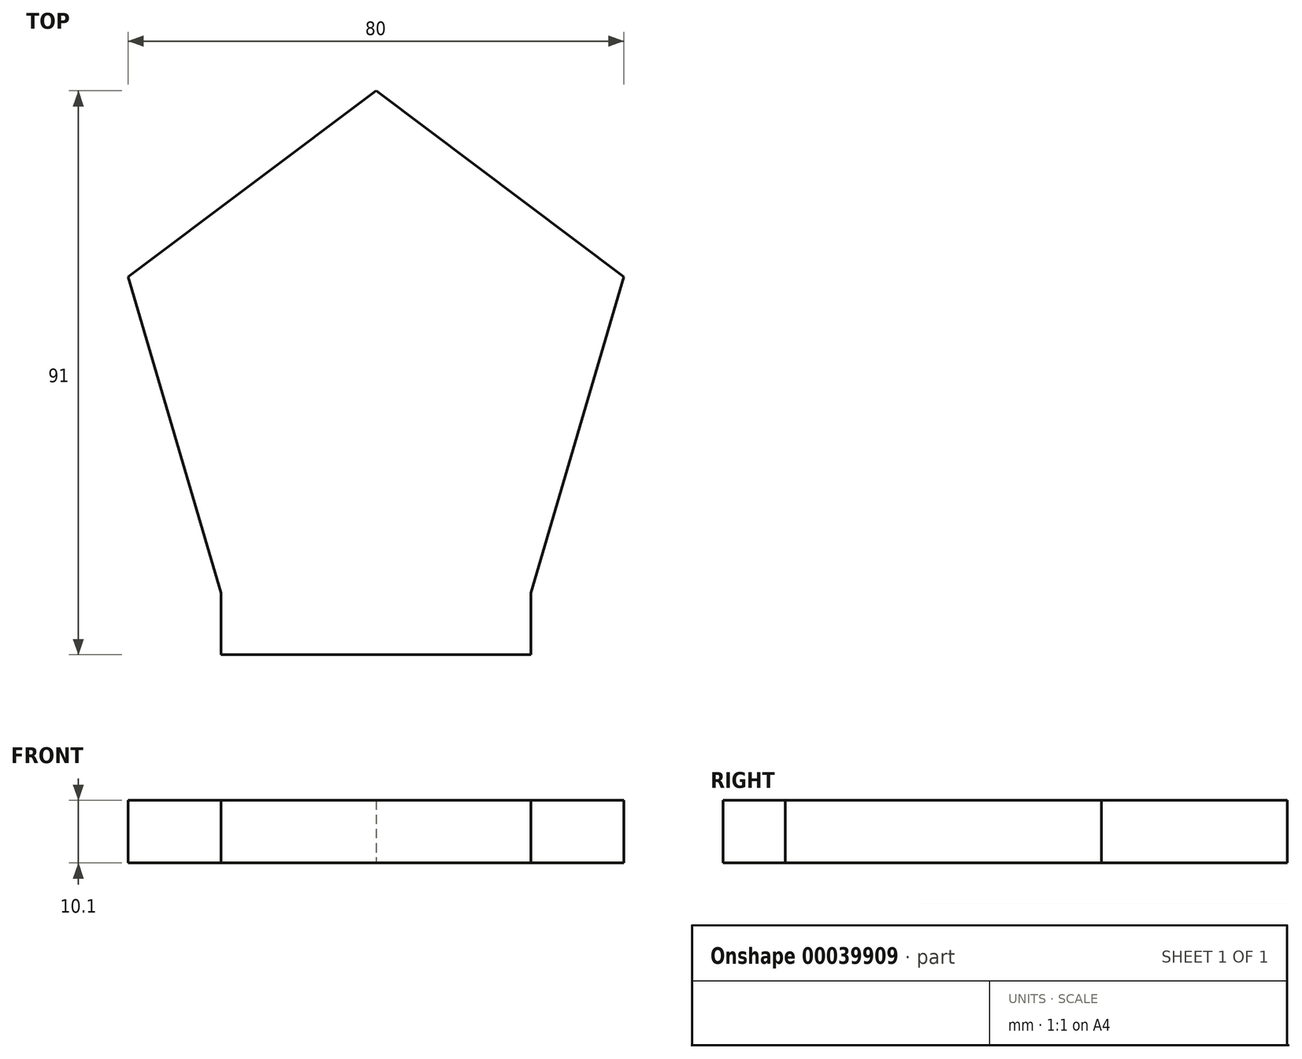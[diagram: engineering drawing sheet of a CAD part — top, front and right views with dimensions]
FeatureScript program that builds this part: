
annotation { "Feature Type Name" : "Feature", "Feature Type Description" : "" }
export const myFeature = defineFeature(function(context is Context, id is Id, definition is map)
    precondition{}
    {
        {
            var Q0;
            Q0=qCreatedBy(makeId("Top.planeOp"),FACE);
            var sketch = newSketch(context, id + "F0", { "sketchPlane" : qUnion([Q0])});
            skLineSegment(sketch, "E0.bottom", {"start": v(-25, -39.07) * mm, "end": v(25, -39.07) * mm});
            skLineSegment(sketch, "E0.top", {"start": v(-25, -49.07) * mm, "end": v(25, -49.07) * mm});
            skLineSegment(sketch, "E0.left", {"start": v(-25, -39.07) * mm, "end": v(-25, -49.07) * mm});
            skLineSegment(sketch, "E0.right", {"start": v(25, -39.07) * mm, "end": v(25, -49.07) * mm});
            skLineSegment(sketch, "E1.top", {"start": v(-25, -69.07) * mm, "end": v(25, -69.07) * mm});
            skLineSegment(sketch, "E1.left", {"start": v(-25, -49.07) * mm, "end": v(-25, -69.07) * mm});
            skLineSegment(sketch, "E1.right", {"start": v(25, -49.07) * mm, "end": v(25, -69.07) * mm});
            skLineSegment(sketch, "E2.bottom", {"start": v(-40, 11.93) * mm, "end": v(40, 11.93) * mm});
            skLineSegment(sketch, "E3", {"start": v(-40, 11.93) * mm, "end": v(-25, -39.07) * mm});
            skLineSegment(sketch, "E4", {"start": v(25, -39.07) * mm, "end": v(40, 11.93) * mm});
            skLineSegment(sketch, "E5", {"start": v(-40, 11.93) * mm, "end": v(0, 41.93) * mm});
            skLineSegment(sketch, "E6", {"start": v(0, 41.93) * mm, "end": v(40, 11.93) * mm});
            skLineSegment(sketch, "E7", {"start": v(0, 41.93) * mm, "end": v(0, 11.93) * mm, "construction": true});
            skLineSegment(sketch, "E8", {"start": v(0, 11.93) * mm, "end": v(0, -39.07) * mm, "construction": true});
            skSolve(sketch);
        }
        {
            var Q0;
            Q0=makeQuery(id+"F0.imprint","IMPRINT",FACE,{"disambiguationData":[TD([[makeQuery(id+"F0.imprint","IMPRINT",EDGE,{"derivedFrom":sQuery(id+"F0.wireOp",EDGE,"E0.bottom")}),1.0]])]});
            var Q1;
            Q1=makeQuery(id+"F0.imprint","IMPRINT",FACE,{"disambiguationData":[TD([[makeQuery(id+"F0.imprint","IMPRINT",EDGE,{"derivedFrom":sQuery(id+"F0.wireOp",EDGE,"E2.bottom")}),1.0]])]});
            var Q2;
            Q2=makeQuery(id+"F0.imprint","IMPRINT",FACE,{"disambiguationData":[TD([[makeQuery(id+"F0.imprint","IMPRINT",EDGE,{"derivedFrom":sQuery(id+"F0.wireOp",EDGE,"E0.bottom")}),-1.0]])]});
            var Q3;
            Q3=makeQuery(id+"F0.imprint","IMPRINT",FACE,{"disambiguationData":[TD([[makeQuery(id+"F0.imprint","IMPRINT",EDGE,{"derivedFrom":sQuery(id+"F0.wireOp",EDGE,"E0.top")}),-1.0]])]});
            extrude(context, id + "F1", {"entities" : qUnion([Q0, Q1, Q2, Q3]), "depth" : 10.1 * mm});
        }
    });
